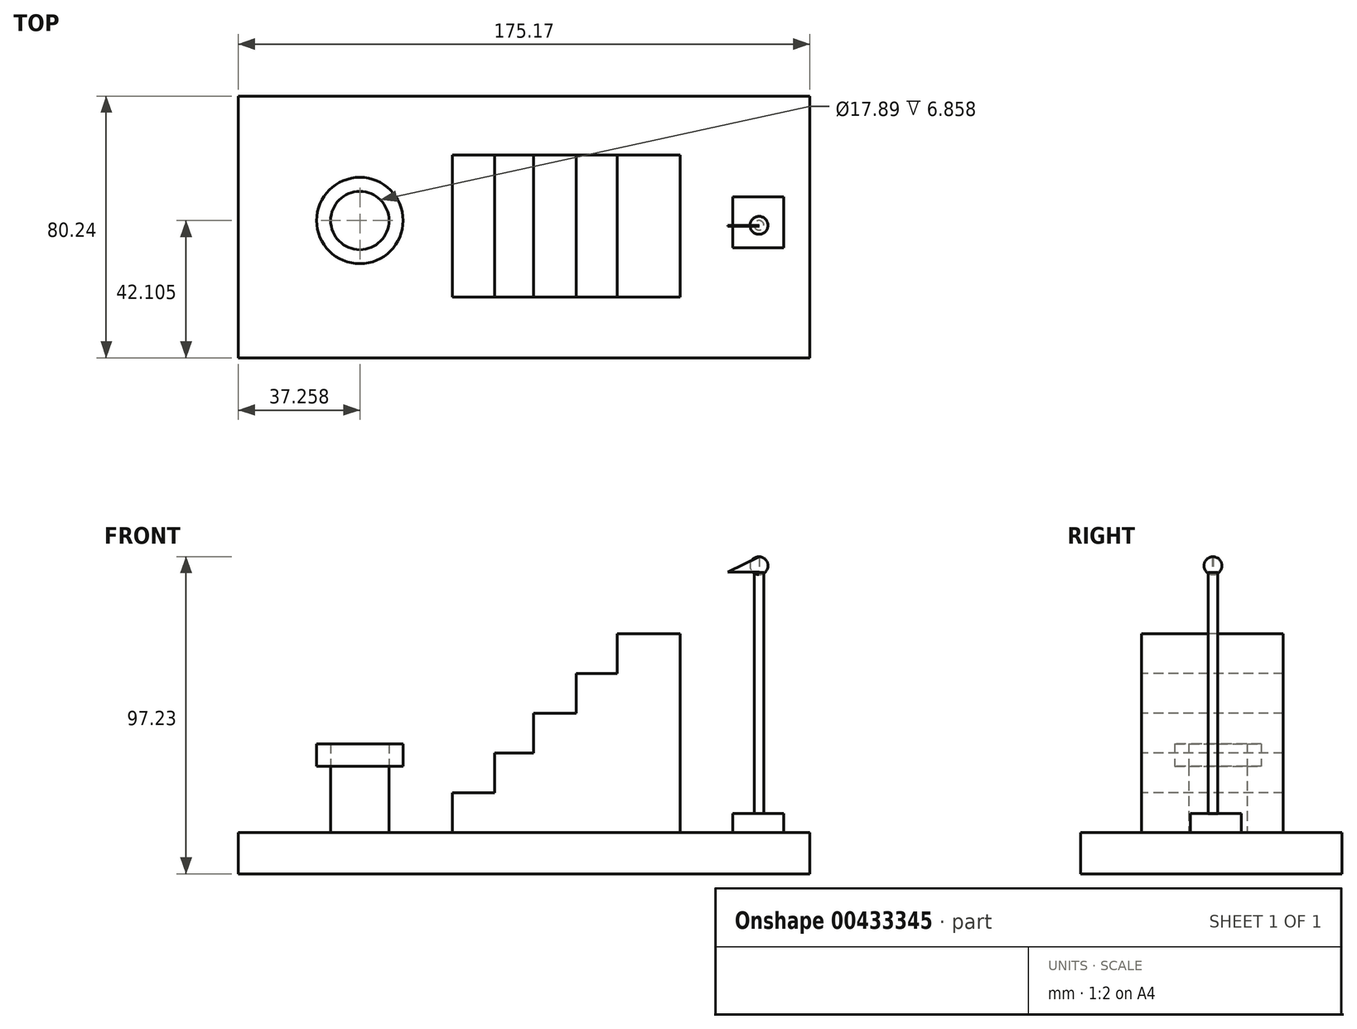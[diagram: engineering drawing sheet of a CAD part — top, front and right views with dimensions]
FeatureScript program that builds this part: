
annotation { "Feature Type Name" : "Feature", "Feature Type Description" : "" }
export const myFeature = defineFeature(function(context is Context, id is Id, definition is map)
    precondition{}
    {
        {
            var Q0;
            Q0=qCreatedBy(makeId("Top.planeOp"),FACE);
            var sketch = newSketch(context, id + "F0", { "sketchPlane" : qUnion([Q0])});
            skLineSegment(sketch, "E0.bottom", {"start": v(-86.67, 39.6) * mm, "end": v(88.5, 39.6) * mm});
            skLineSegment(sketch, "E0.top", {"start": v(-86.67, -40.63) * mm, "end": v(88.5, -40.63) * mm});
            skLineSegment(sketch, "E0.left", {"start": v(-86.67, 39.6) * mm, "end": v(-86.67, -40.63) * mm});
            skLineSegment(sketch, "E0.right", {"start": v(88.5, 39.6) * mm, "end": v(88.5, -40.63) * mm});
            skSolve(sketch);
        }
        {
            var Q0;
            Q0 = qSketchRegion(id + "F0", true);
            extrude(context, id + "F1", {"entities" : qUnion([Q0]), "depth" : 12.7 * mm});
        }
        {
            var Q0;
            Q0=makeQuery(id+"F1.opExtrude","CAP_FACE",FACE,{"disambiguationData":[OSD([sQuery(id+"F0.wireOp",EDGE,"E0.bottom"),sQuery(id+"F0.wireOp",EDGE,"E0.top"),sQuery(id+"F0.wireOp",EDGE,"E0.left"),sQuery(id+"F0.wireOp",EDGE,"E0.right")])],"isStart":false});
            var sketch = newSketch(context, id + "F2", { "sketchPlane" : qUnion([Q0])});
            skCircle(sketch, "E1", {"center": v(-49.41, 1.47) * mm, "radius": 8.94 * mm});
            skLineSegment(sketch, "E2.bottom", {"start": v(-21.4, 21.39) * mm, "end": v(44.42, 21.39) * mm});
            skLineSegment(sketch, "E2.top", {"start": v(-21.4, -20.1) * mm, "end": v(44.42, -20.1) * mm});
            skLineSegment(sketch, "E2.left", {"start": v(-21.4, 21.39) * mm, "end": v(-21.4, -20.1) * mm});
            skLineSegment(sketch, "E2.right", {"start": v(44.42, 21.39) * mm, "end": v(44.42, -20.1) * mm});
            skSolve(sketch);
        }
        {
            var Q0;
            Q0=makeQuery(id+"F2.imprint","IMPRINT",FACE,{"disambiguationData":[TD([[makeQuery(id+"F2.imprint","IMPRINT",EDGE,{"derivedFrom":sQuery(id+"F2.wireOp",EDGE,"E1")}),1.0]])]});
            extrude(context, id + "F3", {"entities" : qUnion([Q0]), "depth" : 20.32 * mm});
        }
        {
            var Q0;
            Q0=makeQuery(id+"F3.opExtrude","CAP_FACE",FACE,{"disambiguationData":[OSD([sQuery(id+"F2.wireOp",EDGE,"E1")])],"isStart":false});
            var sketch = newSketch(context, id + "F4", { "sketchPlane" : qUnion([Q0])});
            skCircle(sketch, "E3", {"center": v(-49.41, 1.47) * mm, "radius": 13.25 * mm});
            skSolve(sketch);
        }
        {
            var Q0;
            Q0=makeQuery(id+"F4.imprint","IMPRINT",FACE,{"disambiguationData":[TD([[makeQuery(id+"F4.imprint","IMPRINT",EDGE,{"derivedFrom":sQuery(id+"F4.wireOp",EDGE,"E3")}),1.0]])]});
            extrude(context, id + "F5", {"entities" : qUnion([Q0]), "depth" : 6.86 * mm});
        }
        {
            var Q0;
            Q0=makeQuery(id+"F1.opExtrude","CAP_FACE",FACE,{"disambiguationData":[OSD([sQuery(id+"F0.wireOp",EDGE,"E0.bottom"),sQuery(id+"F0.wireOp",EDGE,"E0.top"),sQuery(id+"F0.wireOp",EDGE,"E0.left"),sQuery(id+"F0.wireOp",EDGE,"E0.right")])],"isStart":false});
            var sketch = newSketch(context, id + "F6", { "sketchPlane" : qUnion([Q0])});
            skLineSegment(sketch, "E4.bottom", {"start": v(-21.02, 21.57) * mm, "end": v(48.85, 21.57) * mm});
            skLineSegment(sketch, "E4.top", {"start": v(-21.02, -21.94) * mm, "end": v(48.85, -21.94) * mm});
            skLineSegment(sketch, "E4.left", {"start": v(-21.02, 21.57) * mm, "end": v(-21.02, -21.94) * mm});
            skLineSegment(sketch, "E4.right", {"start": v(48.85, 21.57) * mm, "end": v(48.85, -21.94) * mm});
            skSolve(sketch);
        }
        {
            var Q0;
            Q0=makeQuery(id+"F6.imprint","IMPRINT",FACE,{"disambiguationData":[TD([[makeQuery(id+"F6.imprint","IMPRINT",EDGE,{"derivedFrom":sQuery(id+"F6.wireOp",EDGE,"E4.bottom")}),-1.0]])]});
            extrude(context, id + "F7", {"entities" : qUnion([Q0]), "operationType" : NewBodyOperationType.ADD, "depth" : 12.2 * mm});
        }
        {
            var Q0;
            Q0=makeQuery(id+"F7.opExtrude","CAP_FACE",FACE,{"disambiguationData":[OSD([sQuery(id+"F6.wireOp",EDGE,"E4.bottom"),sQuery(id+"F6.wireOp",EDGE,"E4.top"),sQuery(id+"F6.wireOp",EDGE,"E4.left"),sQuery(id+"F6.wireOp",EDGE,"E4.right")])],"isStart":false});
            var sketch = newSketch(context, id + "F8", { "sketchPlane" : qUnion([Q0])});
            skLineSegment(sketch, "E5.bottom", {"start": v(-8.12, 21.57) * mm, "end": v(48.85, 21.57) * mm});
            skLineSegment(sketch, "E5.top", {"start": v(-8.12, -21.94) * mm, "end": v(48.85, -21.94) * mm});
            skLineSegment(sketch, "E5.left", {"start": v(-8.12, 21.57) * mm, "end": v(-8.12, -21.94) * mm});
            skLineSegment(sketch, "E5.right", {"start": v(48.85, 21.57) * mm, "end": v(48.85, -21.94) * mm});
            skSolve(sketch);
        }
        {
            var Q0;
            Q0=makeQuery(id+"F8.imprint","IMPRINT",FACE,{"disambiguationData":[TD([[makeQuery(id+"F8.imprint","IMPRINT",EDGE,{"derivedFrom":sQuery(id+"F8.wireOp",EDGE,"E5.bottom")}),-1.0]])]});
            extrude(context, id + "F9", {"entities" : qUnion([Q0]), "operationType" : NewBodyOperationType.ADD, "depth" : 12.2 * mm});
        }
        {
            var Q0;
            Q0=makeQuery(id+"F9.opExtrude","CAP_FACE",FACE,{"disambiguationData":[OSD([sQuery(id+"F8.wireOp",EDGE,"E5.bottom"),sQuery(id+"F8.wireOp",EDGE,"E5.top"),sQuery(id+"F8.wireOp",EDGE,"E5.left"),sQuery(id+"F8.wireOp",EDGE,"E5.right")])],"isStart":false});
            var sketch = newSketch(context, id + "F10", { "sketchPlane" : qUnion([Q0])});
            skLineSegment(sketch, "E6.bottom", {"start": v(3.9, 21.57) * mm, "end": v(48.85, 21.57) * mm});
            skLineSegment(sketch, "E6.top", {"start": v(3.9, -21.94) * mm, "end": v(48.85, -21.94) * mm});
            skLineSegment(sketch, "E6.left", {"start": v(3.9, 21.57) * mm, "end": v(3.9, -21.94) * mm});
            skLineSegment(sketch, "E6.right", {"start": v(48.85, 21.57) * mm, "end": v(48.85, -21.94) * mm});
            skSolve(sketch);
        }
        {
            var Q0;
            Q0=makeQuery(id+"F10.imprint","IMPRINT",FACE,{"disambiguationData":[TD([[makeQuery(id+"F10.imprint","IMPRINT",EDGE,{"derivedFrom":sQuery(id+"F10.wireOp",EDGE,"E6.bottom")}),-1.0]])]});
            extrude(context, id + "F11", {"entities" : qUnion([Q0]), "operationType" : NewBodyOperationType.ADD, "depth" : 12.2 * mm});
        }
        {
            var Q0;
            Q0=makeQuery(id+"F11.opExtrude","CAP_FACE",FACE,{"disambiguationData":[OSD([sQuery(id+"F10.wireOp",EDGE,"E6.bottom"),sQuery(id+"F10.wireOp",EDGE,"E6.top"),sQuery(id+"F10.wireOp",EDGE,"E6.left"),sQuery(id+"F10.wireOp",EDGE,"E6.right")])],"isStart":false});
            var sketch = newSketch(context, id + "F12", { "sketchPlane" : qUnion([Q0])});
            skLineSegment(sketch, "E7.bottom", {"start": v(16.9, 21.57) * mm, "end": v(48.85, 21.57) * mm});
            skLineSegment(sketch, "E7.top", {"start": v(16.9, -21.94) * mm, "end": v(48.85, -21.94) * mm});
            skLineSegment(sketch, "E7.left", {"start": v(16.9, 21.57) * mm, "end": v(16.9, -21.94) * mm});
            skLineSegment(sketch, "E7.right", {"start": v(48.85, 21.57) * mm, "end": v(48.85, -21.94) * mm});
            skSolve(sketch);
        }
        {
            var Q0;
            Q0=makeQuery(id+"F12.imprint","IMPRINT",FACE,{"disambiguationData":[TD([[makeQuery(id+"F12.imprint","IMPRINT",EDGE,{"derivedFrom":sQuery(id+"F12.wireOp",EDGE,"E7.bottom")}),-1.0]])]});
            extrude(context, id + "F13", {"entities" : qUnion([Q0]), "operationType" : NewBodyOperationType.ADD, "depth" : 12.2 * mm});
        }
        {
            var Q0;
            Q0=makeQuery(id+"F13.opExtrude","CAP_FACE",FACE,{"disambiguationData":[OSD([sQuery(id+"F12.wireOp",EDGE,"E7.bottom"),sQuery(id+"F12.wireOp",EDGE,"E7.top"),sQuery(id+"F12.wireOp",EDGE,"E7.left"),sQuery(id+"F12.wireOp",EDGE,"E7.right")])],"isStart":false});
            var sketch = newSketch(context, id + "F14", { "sketchPlane" : qUnion([Q0])});
            skLineSegment(sketch, "E8.bottom", {"start": v(29.52, 21.57) * mm, "end": v(48.85, 21.57) * mm});
            skLineSegment(sketch, "E8.top", {"start": v(29.52, -21.94) * mm, "end": v(48.85, -21.94) * mm});
            skLineSegment(sketch, "E8.left", {"start": v(29.52, 21.57) * mm, "end": v(29.52, -21.94) * mm});
            skLineSegment(sketch, "E8.right", {"start": v(48.85, 21.57) * mm, "end": v(48.85, -21.94) * mm});
            skSolve(sketch);
        }
        {
            var Q0;
            Q0=makeQuery(id+"F14.imprint","IMPRINT",FACE,{"disambiguationData":[TD([[makeQuery(id+"F14.imprint","IMPRINT",EDGE,{"derivedFrom":sQuery(id+"F14.wireOp",EDGE,"E8.bottom")}),-1.0]])]});
            extrude(context, id + "F15", {"entities" : qUnion([Q0]), "operationType" : NewBodyOperationType.ADD, "depth" : 12.2 * mm});
        }
        {
            var Q0;
            Q0=makeQuery(id+"F1.opExtrude","CAP_FACE",FACE,{"disambiguationData":[OSD([sQuery(id+"F0.wireOp",EDGE,"E0.bottom"),sQuery(id+"F0.wireOp",EDGE,"E0.top"),sQuery(id+"F0.wireOp",EDGE,"E0.left"),sQuery(id+"F0.wireOp",EDGE,"E0.right")])],"isStart":false});
            var sketch = newSketch(context, id + "F16", { "sketchPlane" : qUnion([Q0])});
            skLineSegment(sketch, "E9.bottom", {"start": v(64.93, 8.7) * mm, "end": v(80.5, 8.7) * mm});
            skLineSegment(sketch, "E9.top", {"start": v(64.93, -6.9) * mm, "end": v(80.5, -6.9) * mm});
            skLineSegment(sketch, "E9.left", {"start": v(64.93, 8.7) * mm, "end": v(64.93, -6.9) * mm});
            skLineSegment(sketch, "E9.right", {"start": v(80.5, 8.7) * mm, "end": v(80.5, -6.9) * mm});
            skSolve(sketch);
        }
        {
            var Q0;
            Q0=makeQuery(id+"F16.imprint","IMPRINT",FACE,{"disambiguationData":[TD([[makeQuery(id+"F16.imprint","IMPRINT",EDGE,{"derivedFrom":sQuery(id+"F16.wireOp",EDGE,"E9.bottom")}),-1.0]])]});
            extrude(context, id + "F17", {"entities" : qUnion([Q0]), "operationType" : NewBodyOperationType.ADD, "depth" : 5.84 * mm});
        }
        {
            var Q0;
            Q0=qCreatedBy(makeId("Front.planeOp"),FACE);
            var sketch = newSketch(context, id + "F18", { "sketchPlane" : qUnion([Q0])});
            skLineSegment(sketch, "E10.bottom", {"start": v(71.52, 92.36) * mm, "end": v(73, 92.36) * mm});
            skLineSegment(sketch, "E10.top", {"start": v(71.52, 18.25) * mm, "end": v(73, 18.25) * mm});
            skLineSegment(sketch, "E10.left", {"start": v(71.52, 92.36) * mm, "end": v(71.52, 18.25) * mm});
            skLineSegment(sketch, "E10.right", {"start": v(73, 92.36) * mm, "end": v(73, 18.25) * mm});
            skSolve(sketch);
        }
        {
            var Q0;
            Q0=makeQuery(id+"F18.imprint","IMPRINT",FACE,{"disambiguationData":[TD([[makeQuery(id+"F18.imprint","IMPRINT",EDGE,{"derivedFrom":sQuery(id+"F18.wireOp",EDGE,"E10.bottom")}),-1.0]])]});
            var Q1;
            Q1=sQuery(id+"F18.wireOp",EDGE,"E10.right");
            revolve(context, id + "F19", {"entities" : qUnion([Q0]), "axis" : qUnion([Q1]), "revolveType" : RevolveType.FULL});
        }
        {
            var Q0;
            Q0=qCreatedBy(makeId("Front.planeOp"),FACE);
            var sketch = newSketch(context, id + "F20", { "sketchPlane" : qUnion([Q0])});
            skLineSegment(sketch, "E11", {"start": v(73, 91.72) * mm, "end": v(73, 97.23) * mm});
            skArc(sketch, "E12", {"start": v(73, 97.23) * mm, "mid": v(70.24, 94.47) * mm, "end": v(73, 91.72) * mm});
            skSolve(sketch);
        }
        {
            var Q0;
            Q0=makeQuery(id+"F20.imprint","IMPRINT",FACE,{"disambiguationData":[TD([[makeQuery(id+"F20.imprint","IMPRINT",EDGE,{"derivedFrom":sQuery(id+"F20.wireOp",EDGE,"E11")}),1.0]])]});
            var Q1;
            Q1=sQuery(id+"F20.wireOp",EDGE,"E11");
            revolve(context, id + "F21", {"entities" : qUnion([Q0]), "axis" : qUnion([Q1]), "revolveType" : RevolveType.FULL});
        }
        {
            var Q0;
            Q0=qCreatedBy(makeId("Front.planeOp"),FACE);
            var sketch = newSketch(context, id + "F22", { "sketchPlane" : qUnion([Q0])});
            skLineSegment(sketch, "E13", {"start": v(73.02, 97.18) * mm, "end": v(63.37, 92.48) * mm});
            skLineSegment(sketch, "E14", {"start": v(73.02, 92.5) * mm, "end": v(63.37, 92.48) * mm});
            skLineSegment(sketch, "E15", {"start": v(73.02, 97.18) * mm, "end": v(73.02, 92.5) * mm});
            skSolve(sketch);
        }
        {
            var Q0;
            Q0=makeQuery(id+"F22.imprint","IMPRINT",FACE,{"disambiguationData":[TD([[makeQuery(id+"F22.imprint","IMPRINT",EDGE,{"derivedFrom":sQuery(id+"F22.wireOp",EDGE,"E13")}),1.0]])]});
            extrude(context, id + "F23", {"entities" : qUnion([Q0]), "depth" : 0.25 * mm});
        }
    });
